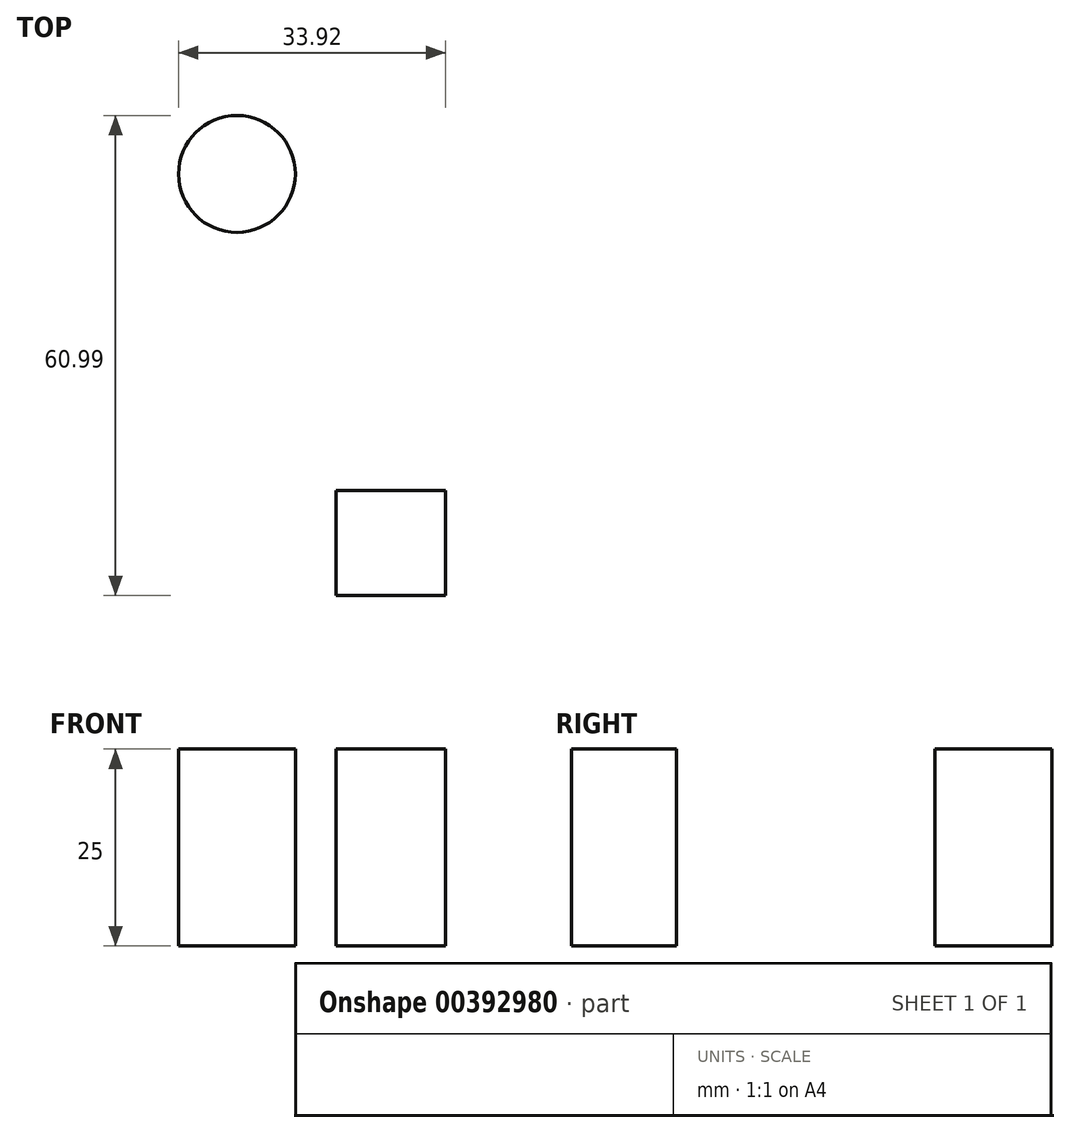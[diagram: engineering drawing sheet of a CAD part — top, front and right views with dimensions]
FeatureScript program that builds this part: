
annotation { "Feature Type Name" : "Feature", "Feature Type Description" : "" }
export const myFeature = defineFeature(function(context is Context, id is Id, definition is map)
    precondition{}
    {
        {
            var Q0;
            Q0=qCreatedBy(makeId("Top.planeOp"),FACE);
            var sketch = newSketch(context, id + "F0", { "sketchPlane" : qUnion([Q0])});
            skArc(sketch, "E0", {"start": v(-40.2, 18.4) * mm, "mid": v(-38.7, 22.34) * mm, "end": v(-39, 26.55) * mm});
            skFitSpline(sketch, "E1", {"points": [v(-39, 26.55) * mm, v(-30.52, 36.39) * mm, v(-14.95, 21.37) * mm, v(-25.51, 5.8) * mm, v(-19.2, -13.3) * mm, v(-27, -26.08) * mm], "startDerivative": vector(34.74, 86.54) * mm, "endDerivative": vector(-67.72, -62.81) * mm});
            skLineSegment(sketch, "E2.bottom", {"start": v(-33.67, -26.08) * mm, "end": v(-19.77, -26.08) * mm});
            skLineSegment(sketch, "E2.top", {"start": v(-33.67, -39.43) * mm, "end": v(-19.77, -39.43) * mm});
            skLineSegment(sketch, "E2.left", {"start": v(-33.67, -26.08) * mm, "end": v(-33.67, -39.43) * mm});
            skLineSegment(sketch, "E2.right", {"start": v(-19.77, -26.08) * mm, "end": v(-19.77, -39.43) * mm});
            skCircle(sketch, "E3", {"center": v(-46.27, 14.14) * mm, "radius": 7.42 * mm});
            skSolve(sketch);
        }
        {
            var Q0;
            Q0=makeQuery(id+"F0.imprint","IMPRINT",FACE,{"disambiguationData":[TD([[makeQuery(id+"F0.imprint","IMPRINT",EDGE,{"derivedFrom":sQuery(id+"F0.wireOp",EDGE,"E3")}),1.0]])]});
            var Q1;
            Q1=makeQuery(id+"F0.imprint","IMPRINT",FACE,{"disambiguationData":[TD([[makeQuery(id+"F0.imprint","IMPRINT",EDGE,{"derivedFrom":sQuery(id+"F0.wireOp",EDGE,"E2.top")}),1.0]])]});
            var Q2;
            Q2=sQuery(id+"F0.wireOp",EDGE,"E3");
            extrude(context, id + "F1", {"entities" : qUnion([Q0, Q1]), "surfaceEntities" : qUnion([Q2]), "depth" : 25 * mm});
        }
        {
            var Q0;
            Q0=qCreatedBy(makeId("Top.planeOp"),FACE);
            var sketch = newSketch(context, id + "F2", { "sketchPlane" : qUnion([Q0])});
            skCircle(sketch, "E4.0", {"center": v(-46.27, 14.14) * mm, "radius": 7.42 * mm});
            skLineSegment(sketch, "E5.0", {"start": v(-19.77, -26.08) * mm, "end": v(-19.77, -39.43) * mm});
            skFitSpline(sketch, "E6", {"points": [v(-39.81, 17.79) * mm, v(-19.82, 20.25) * mm, v(-4.22, -6.79) * mm, v(-9.11, -27.3) * mm, v(-19.77, -32.75) * mm], "startDerivative": vector(83.83, 33.05) * mm, "endDerivative": vector(-60.77, -18.43) * mm});
            skSolve(sketch);
        }
        {
            var Q0;
            Q0=sQuery(id+"F2.wireOp",EDGE,"E6");
            cPlane(context, id + "F3", {"entities" : qUnion([Q0]), "cplaneType" : CPlaneType.MID_PLANE, "offset" : 25 * mm, "width" : 150 * mm, "height" : 150 * mm});
        }
    });
